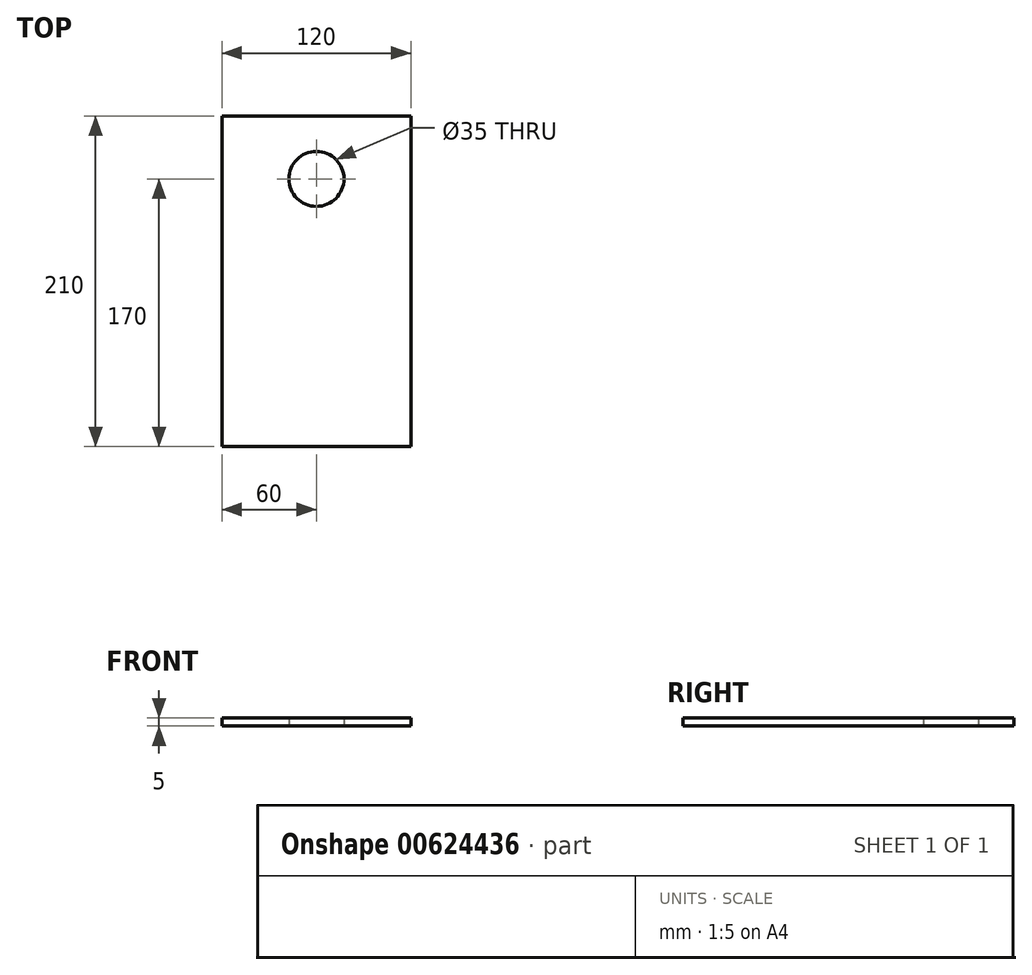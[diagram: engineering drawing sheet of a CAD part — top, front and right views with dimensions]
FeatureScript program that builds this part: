
annotation { "Feature Type Name" : "Feature", "Feature Type Description" : "" }
export const myFeature = defineFeature(function(context is Context, id is Id, definition is map)
    precondition{}
    {
        {
            var Q0;
            Q0=qCreatedBy(makeId("Top.planeOp"),FACE);
            var sketch = newSketch(context, id + "F0", { "sketchPlane" : qUnion([Q0])});
            skLineSegment(sketch, "E0.bottom", {"start": v(60, -105) * mm, "end": v(-60, -105) * mm});
            skLineSegment(sketch, "E0.top", {"start": v(60, 105) * mm, "end": v(-60, 105) * mm});
            skLineSegment(sketch, "E0.left", {"start": v(60, -105) * mm, "end": v(60, 105) * mm});
            skLineSegment(sketch, "E0.right", {"start": v(-60, -105) * mm, "end": v(-60, 105) * mm});
            skPoint(sketch, "E0.middle", {"position": v(0, 0) * mm});
            skPoint(sketch, "E1.endSnap0", {"position": v(0, 105) * mm});
            skCircle(sketch, "E2", {"center": v(0, 65) * mm, "radius": 17.5 * mm});
            skSolve(sketch);
        }
        {
            var Q0;
            Q0 = qSketchRegion(id + "F0", true);
            extrude(context, id + "F1", {"entities" : qUnion([Q0]), "depth" : 5 * mm, "offsetDistance" : 25.4 * mm});
        }
    });
